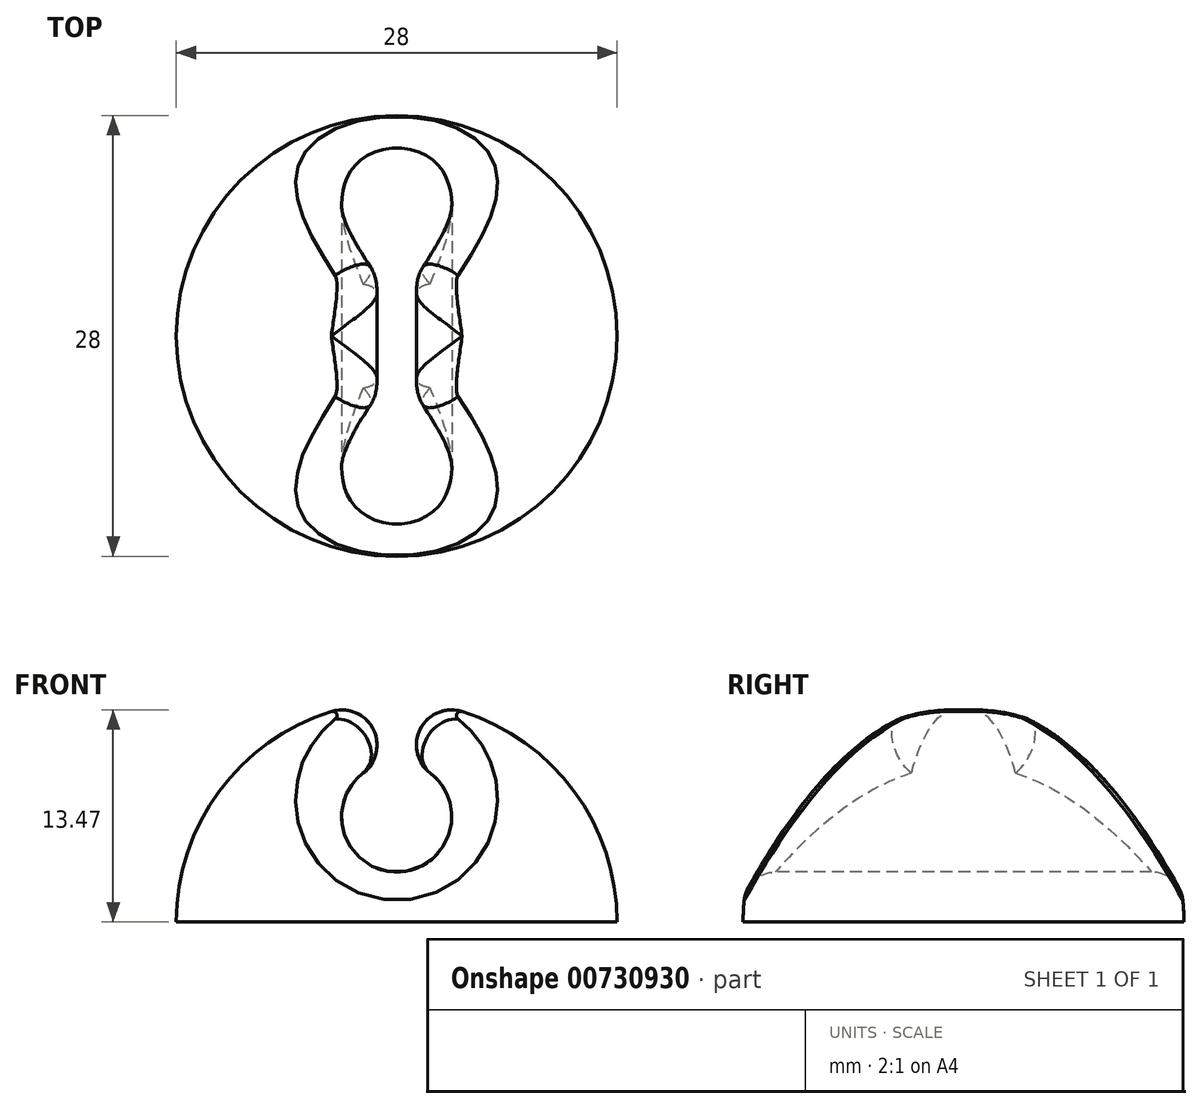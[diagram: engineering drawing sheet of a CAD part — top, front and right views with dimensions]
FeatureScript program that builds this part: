
annotation { "Feature Type Name" : "Feature", "Feature Type Description" : "" }
export const myFeature = defineFeature(function(context is Context, id is Id, definition is map)
    precondition{}
    {
        {
            var Q0;
            Q0=qCreatedBy(makeId("Top.planeOp"),FACE);
            var sketch = newSketch(context, id + "F0", { "sketchPlane" : qUnion([Q0])});
            skArc(sketch, "E0", {"start": v(0, 14) * mm, "mid": v(-14, 0) * mm, "end": v(0, -14) * mm});
            skLineSegment(sketch, "E1", {"start": v(0, 14) * mm, "end": v(0, -14) * mm});
            skPoint(sketch, "E2", {"position": v(-14, 0) * mm});
            skSolve(sketch);
        }
        {
            var Q0;
            Q0 = qSketchRegion(id + "F0", true);
            var Q1;
            Q1=sQuery(id+"F0.wireOp",EDGE,"E1");
            revolve(context, id + "F1", {"surfaceOperationType" : NewSurfaceOperationType.NEW, "entities" : qUnion([Q0]), "axis" : qUnion([Q1]), "revolveType" : RevolveType.ONE_DIRECTION, "oppositeDirection" : true, "angle" : 180 * degree});
        }
        {
            var Q0;
            Q0=qCreatedBy(makeId("Front.planeOp"),FACE);
            var sketch = newSketch(context, id + "F2", { "sketchPlane" : qUnion([Q0])});
            skCircle(sketch, "E3", {"center": v(0, 6.68) * mm, "radius": 3.5 * mm});
            skArc(sketch, "E4", {"start": v(-2.13, 9.45) * mm, "mid": v(-1.5, 12.26) * mm, "end": v(-4.15, 13.37) * mm});
            skArc(sketch, "E5", {"start": v(-14, 0) * mm, "mid": v(0, 14) * mm, "end": v(14, 0) * mm});
            skArc(sketch, "E6", {"start": v(4.15, 13.37) * mm, "mid": v(1.5, 12.26) * mm, "end": v(2.13, 9.45) * mm});
            skLineSegment(sketch, "E7", {"start": v(-2.13, 9.45) * mm, "end": v(2.13, 9.45) * mm, "construction": true});
            skSolve(sketch);
        }
        {
            var Q0;
            {var subQ0=sQuery(id+"F2.wireOp",EDGE,"E3");var subQ1=makeQuery(id+"F2.imprint","INTERSECT",VERTEX,{"derivedFrom":[subQ0,sQuery(id+"F2.wireOp",EDGE,"E4")]});Q0=makeQuery(id+"F2.imprint","IMPRINT",FACE,{"disambiguationData":[TD([[makeQuery(id+"F2.imprint","IMPRINT",EDGE,{"disambiguationData":[TD([[subQ1,1.0]])],"derivedFrom":subQ0}),1.0]])]});}
            var Q1;
            {var subQ0=sQuery(id+"F2.wireOp",EDGE,"E4");Q1=makeQuery(id+"F2.imprint","IMPRINT",FACE,{"disambiguationData":[TD([[makeQuery(id+"F2.imprint","IMPRINT",EDGE,{"derivedFrom":subQ0}),-1.0]])]});}
            extrude(context, id + "F3", {"entities" : qUnion([Q0, Q1]), "operationType" : NewBodyOperationType.REMOVE, "oppositeDirection" : true, "depth" : 30 * mm, "offsetDistance" : 25 * mm, "symmetric" : true});
        }
        {
            var Q0;
            Q0=makeQuery(id+"F3.boolean.opBoolean","INTERSECT",EDGE,{"disambiguationData":[OD(0.0)],"derivedFrom":[makeQuery(id+"F1.opRevolve","SWEPT_FACE",FACE,{"disambiguationData":[OSD([sQuery(id+"F0.wireOp",EDGE,"E0")])]}),makeQuery(id+"F3.opExtrude","SWEPT_FACE",FACE,{"disambiguationData":[OSD([sQuery(id+"F2.wireOp",EDGE,"E3")])]})]});
            var Q1;
            Q1=makeQuery(id+"F3.boolean.opBoolean","INTERSECT",EDGE,{"disambiguationData":[OD(1.0)],"derivedFrom":[makeQuery(id+"F1.opRevolve","SWEPT_FACE",FACE,{"disambiguationData":[OSD([sQuery(id+"F0.wireOp",EDGE,"E0")])]}),makeQuery(id+"F3.opExtrude","SWEPT_FACE",FACE,{"disambiguationData":[OSD([sQuery(id+"F2.wireOp",EDGE,"E3")])]})]});
            fillet(context, id + "F4", {"entities" : qUnion([Q0, Q1]), "radius" : 2 * mm, "tangentPropagation" : true, "allowEdgeOverflow" : false});
        }
    });
